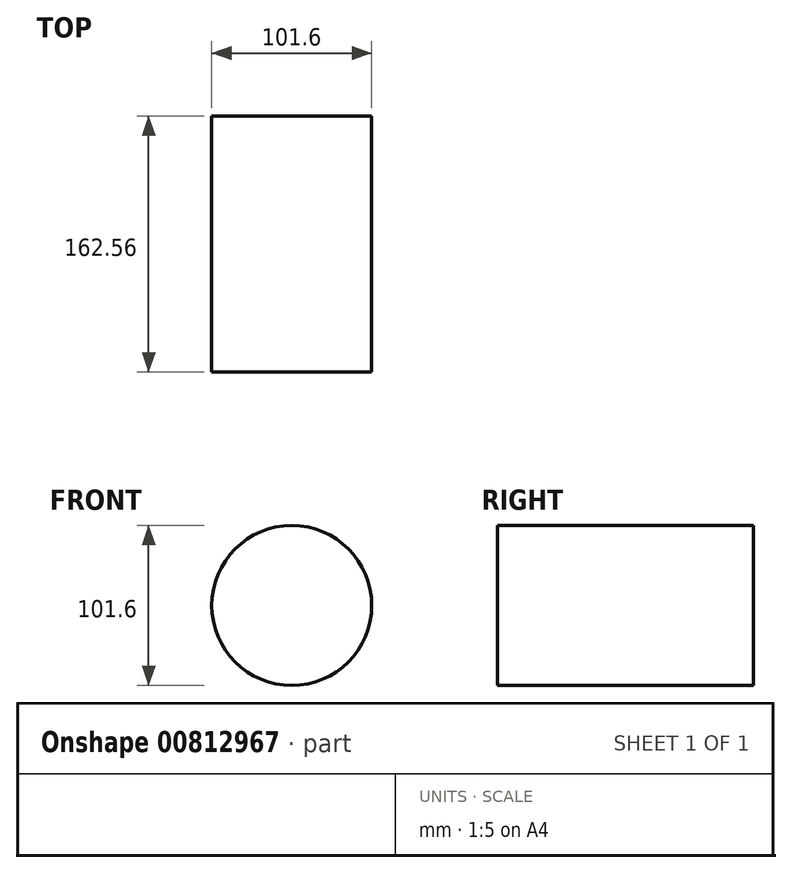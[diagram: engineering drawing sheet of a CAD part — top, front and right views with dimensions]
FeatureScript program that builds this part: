
annotation { "Feature Type Name" : "Feature", "Feature Type Description" : "" }
export const myFeature = defineFeature(function(context is Context, id is Id, definition is map)
    precondition{}
    {
        {
            var Q0;
            Q0=qCreatedBy(makeId("Front.planeOp"),FACE);
            var sketch = newSketch(context, id + "F0", { "sketchPlane" : qUnion([Q0])});
            skCircle(sketch, "E0", {"center": v(0, 0) * mm, "radius": 50.8 * mm});
            skSolve(sketch);
        }
        {
            var Q0;
            Q0 = qSketchRegion(id + "F0", true);
            extrude(context, id + "F1", {"entities" : qUnion([Q0]), "depth" : 162.56 * mm, "offsetDistance" : 25.4 * mm});
        }
    });
